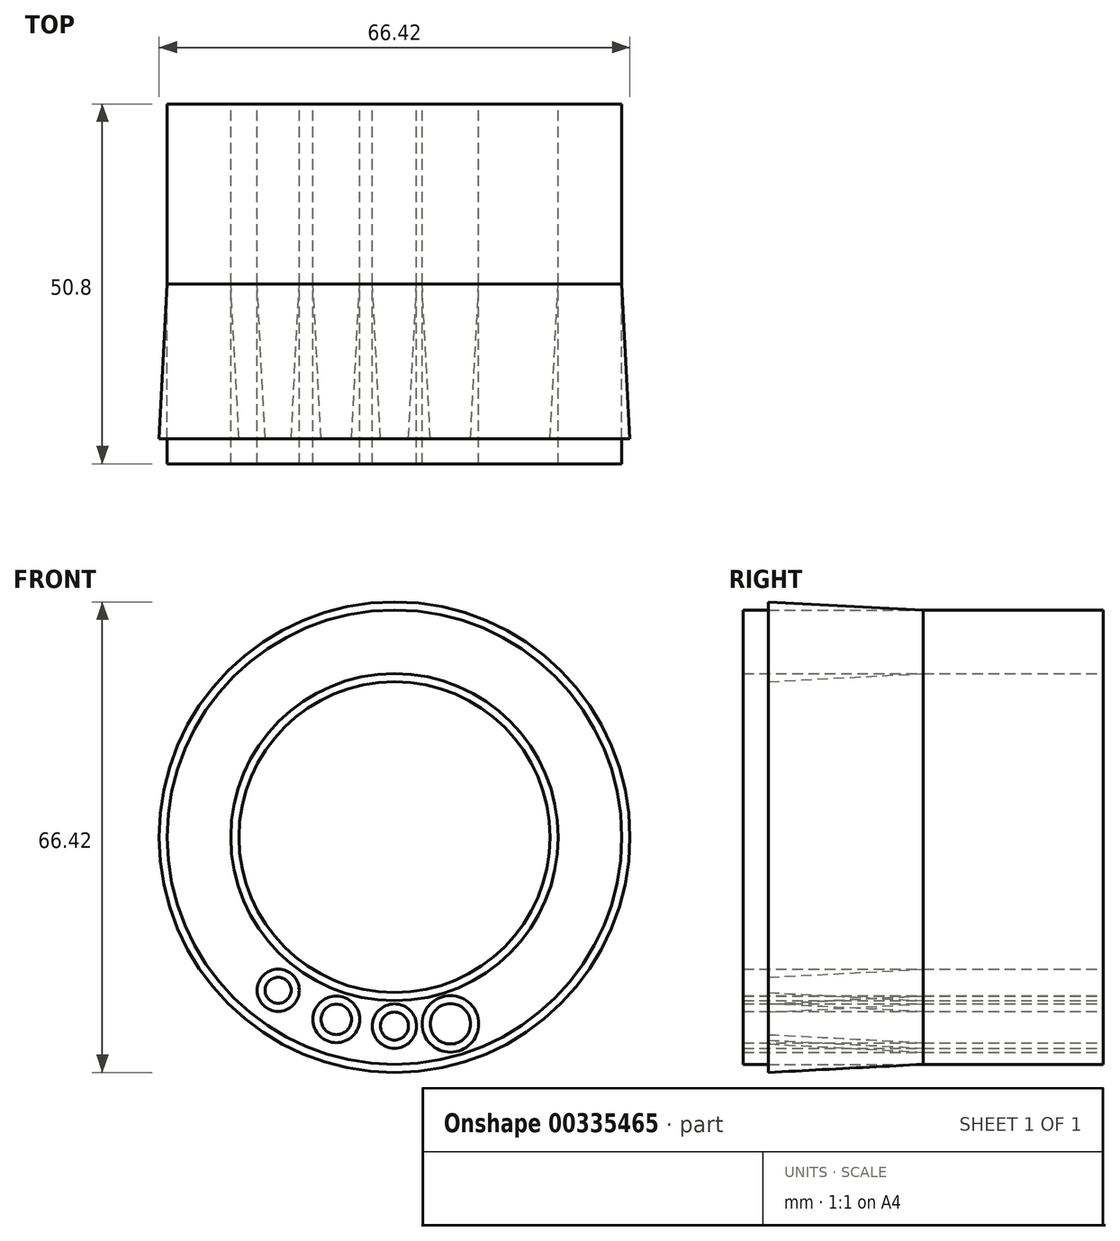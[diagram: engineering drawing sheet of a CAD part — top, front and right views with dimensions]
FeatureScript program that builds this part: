
annotation { "Feature Type Name" : "Feature", "Feature Type Description" : "" }
export const myFeature = defineFeature(function(context is Context, id is Id, definition is map)
    precondition{}
    {
        {
            var Q0;
            Q0=qCreatedBy(makeId("Front.planeOp"),FACE);
            var sketch = newSketch(context, id + "F0", { "sketchPlane" : qUnion([Q0])});
            skCircle(sketch, "E0", {"center": v(0, 0) * mm, "radius": 32.07 * mm});
            skCircle(sketch, "E1", {"center": v(0, 0) * mm, "radius": 23.1 * mm});
            skCircle(sketch, "E2", {"center": v(-16.41, -21.62) * mm, "radius": 2.98 * mm});
            skCircle(sketch, "E3", {"center": v(-16.41, -21.62) * mm, "radius": 2.47 * mm});
            skCircle(sketch, "E4", {"center": v(-8.2, -25.72) * mm, "radius": 3.3 * mm});
            skCircle(sketch, "E5", {"center": v(0, -26.67) * mm, "radius": 3.12 * mm});
            skCircle(sketch, "E6", {"center": v(7.9, -26.35) * mm, "radius": 4 * mm});
            skSolve(sketch);
        }
        {
            var Q0;
            Q0 = qSketchRegion(id + "F0", true);
            extrude(context, id + "F1", {"entities" : qUnion([Q0]), "depth" : 21.84 * mm, "hasDraft" : true, "draftAngle" : 3 * degree, "hasSecondDirection" : true, "secondDirectionOppositeDirection" : true, "secondDirectionDepth" : 25.4 * mm});
        }
        {
            var Q0;
            Q0=makeQuery(id+"F0.imprint","IMPRINT",FACE,{"disambiguationData":[TD([[makeQuery(id+"F0.imprint","IMPRINT",EDGE,{"derivedFrom":sQuery(id+"F0.wireOp",EDGE,"E0")}),1.0]])]});
            extrude(context, id + "F2", {"entities" : qUnion([Q0]), "depth" : 25.4 * mm});
        }
    });
